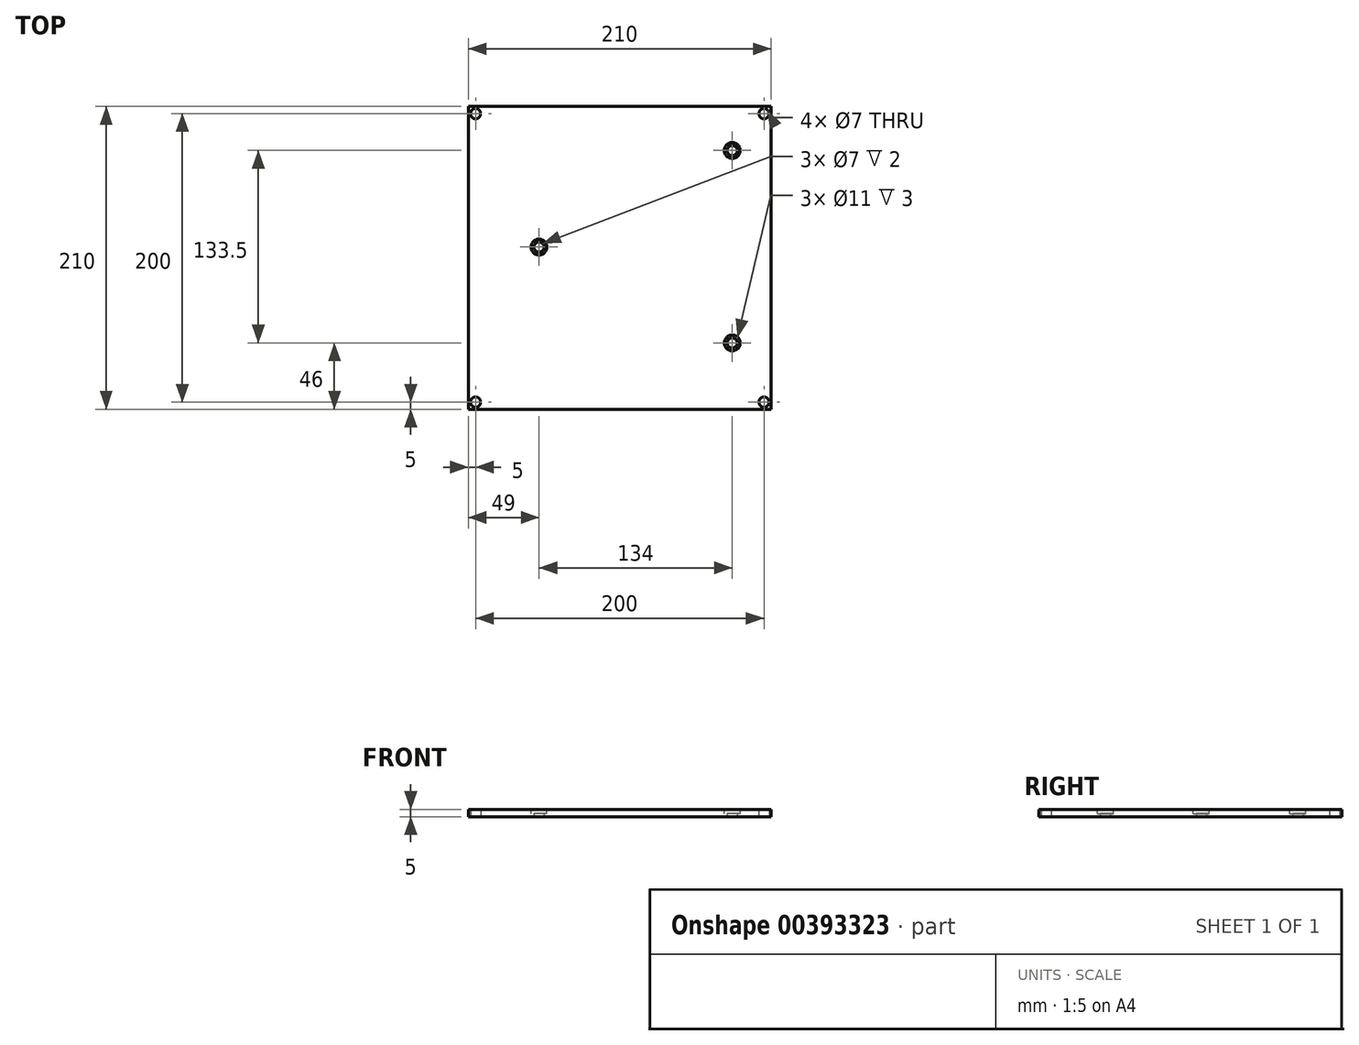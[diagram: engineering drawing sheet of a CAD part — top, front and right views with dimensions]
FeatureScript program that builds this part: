
annotation { "Feature Type Name" : "Feature", "Feature Type Description" : "" }
export const myFeature = defineFeature(function(context is Context, id is Id, definition is map)
    precondition{}
    {
        {
            var Q0;
            Q0=qCreatedBy(makeId("Top.planeOp"),FACE);
            var sketch = newSketch(context, id + "F0", { "sketchPlane" : qUnion([Q0])});
            skLineSegment(sketch, "E0.bottom", {"start": v(-105, 105) * mm, "end": v(105, 105) * mm});
            skLineSegment(sketch, "E0.top", {"start": v(-105, -105) * mm, "end": v(105, -105) * mm});
            skLineSegment(sketch, "E0.left", {"start": v(-105, 105) * mm, "end": v(-105, -105) * mm});
            skLineSegment(sketch, "E0.right", {"start": v(105, 105) * mm, "end": v(105, -105) * mm});
            skCircle(sketch, "E1", {"center": v(-56, 7.5) * mm, "radius": 3.5 * mm});
            skCircle(sketch, "E2", {"center": v(78, 74.5) * mm, "radius": 3.5 * mm});
            skCircle(sketch, "E3", {"center": v(78, -59) * mm, "radius": 3.5 * mm});
            skCircle(sketch, "E4", {"center": v(-100, 100) * mm, "radius": 3.5 * mm});
            skCircle(sketch, "E5", {"center": v(-100, -100) * mm, "radius": 3.5 * mm});
            skCircle(sketch, "E6", {"center": v(100, -100) * mm, "radius": 3.5 * mm});
            skCircle(sketch, "E7", {"center": v(100, 100) * mm, "radius": 3.5 * mm});
            skSolve(sketch);
        }
        {
            var Q0;
            Q0 = qSketchRegion(id + "F0", true);
            extrude(context, id + "F1", {"entities" : qUnion([Q0]), "depth" : 5 * mm});
        }
        {
            var Q0;
            Q0=makeQuery(id+"F1.opExtrude","CAP_FACE",FACE,{"disambiguationData":[OSD([sQuery(id+"F0.wireOp",EDGE,"E0.bottom"),sQuery(id+"F0.wireOp",EDGE,"E0.top"),sQuery(id+"F0.wireOp",EDGE,"E0.left"),sQuery(id+"F0.wireOp",EDGE,"E0.right"),sQuery(id+"F0.wireOp",EDGE,"E1"),sQuery(id+"F0.wireOp",EDGE,"E2"),sQuery(id+"F0.wireOp",EDGE,"E3"),sQuery(id+"F0.wireOp",EDGE,"E4"),sQuery(id+"F0.wireOp",EDGE,"E5"),sQuery(id+"F0.wireOp",EDGE,"E6"),sQuery(id+"F0.wireOp",EDGE,"E7")])],"isStart":false});
            var sketch = newSketch(context, id + "F2", { "sketchPlane" : qUnion([Q0])});
            skCircle(sketch, "E8", {"center": v(-56, 7.5) * mm, "radius": 5.5 * mm});
            skCircle(sketch, "E9", {"center": v(78, 74.5) * mm, "radius": 5.5 * mm});
            skCircle(sketch, "E10", {"center": v(78, -59) * mm, "radius": 5.5 * mm});
            skSolve(sketch);
        }
        {
            var Q0;
            Q0 = qSketchRegion(id + "F2", true);
            extrude(context, id + "F3", {"entities" : qUnion([Q0]), "operationType" : NewBodyOperationType.REMOVE, "oppositeDirection" : true, "depth" : 3 * mm});
        }
    });
